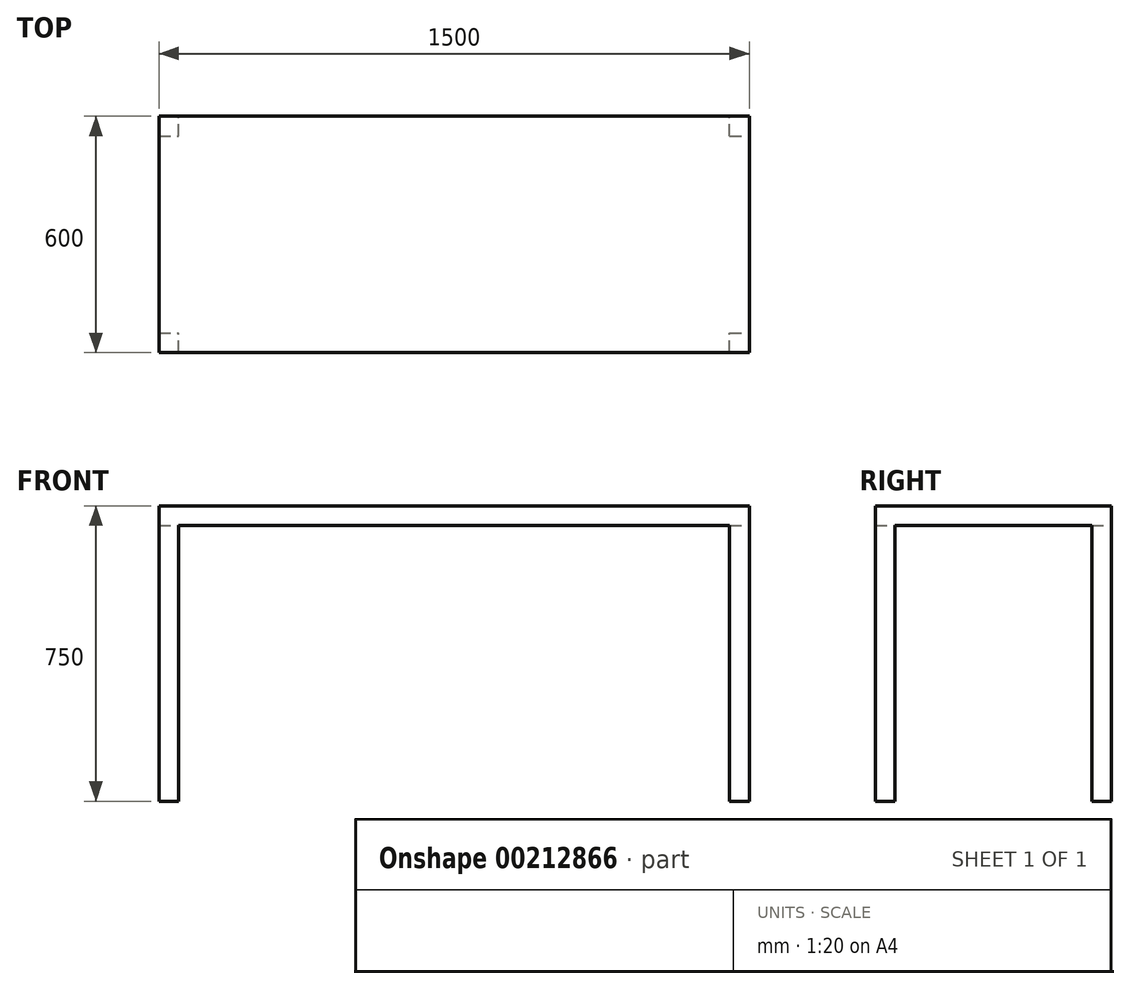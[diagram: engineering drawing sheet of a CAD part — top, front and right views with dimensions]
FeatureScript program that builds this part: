
annotation { "Feature Type Name" : "Feature", "Feature Type Description" : "" }
export const myFeature = defineFeature(function(context is Context, id is Id, definition is map)
    precondition{}
    {
        {
            var Q0;
            Q0=qCreatedBy(makeId("Top.planeOp"),FACE);
            var sketch = newSketch(context, id + "F0", { "sketchPlane" : qUnion([Q0])});
            skLineSegment(sketch, "E0.bottom", {"start": v(0, 600) * mm, "end": v(1500, 600) * mm});
            skLineSegment(sketch, "E0.top", {"start": v(0, 0) * mm, "end": v(1500, 0) * mm});
            skLineSegment(sketch, "E0.left", {"start": v(0, 600) * mm, "end": v(0, 0) * mm});
            skLineSegment(sketch, "E0.right", {"start": v(1500, 600) * mm, "end": v(1500, 0) * mm});
            skSolve(sketch);
        }
        {
            var Q0;
            Q0 = qSketchRegion(id + "F0", true);
            extrude(context, id + "F1", {"entities" : qUnion([Q0]), "depth" : 50 * mm});
        }
        {
            var Q0;
            Q0=makeQuery(id+"F1.opExtrude","CAP_FACE",FACE,{"disambiguationData":[OSD([sQuery(id+"F0.wireOp",EDGE,"E0.bottom"),sQuery(id+"F0.wireOp",EDGE,"E0.top"),sQuery(id+"F0.wireOp",EDGE,"E0.left"),sQuery(id+"F0.wireOp",EDGE,"E0.right")])],"isStart":true});
            var sketch = newSketch(context, id + "F2", { "sketchPlane" : qUnion([Q0])});
            skLineSegment(sketch, "E1.bottom", {"start": v(0, 0) * mm, "end": v(50, 0) * mm});
            skLineSegment(sketch, "E1.top", {"start": v(0, -50) * mm, "end": v(50, -50) * mm});
            skLineSegment(sketch, "E1.left", {"start": v(0, 0) * mm, "end": v(0, -50) * mm});
            skLineSegment(sketch, "E1.right", {"start": v(50, 0) * mm, "end": v(50, -50) * mm});
            skLineSegment(sketch, "E2.0.1.0", {"start": v(50, -550) * mm, "end": v(50, -600) * mm});
            skLineSegment(sketch, "E2.0.1.1", {"start": v(0, -550) * mm, "end": v(50, -550) * mm});
            skLineSegment(sketch, "E2.0.1.2", {"start": v(0, -550) * mm, "end": v(0, -600) * mm});
            skLineSegment(sketch, "E2.0.1.3", {"start": v(0, -600) * mm, "end": v(50, -600) * mm});
            skLineSegment(sketch, "E2.1.0.0", {"start": v(1500, 0) * mm, "end": v(1500, -50) * mm});
            skLineSegment(sketch, "E2.1.0.1", {"start": v(1450, 0) * mm, "end": v(1500, 0) * mm});
            skLineSegment(sketch, "E2.1.0.2", {"start": v(1450, 0) * mm, "end": v(1450, -50) * mm});
            skLineSegment(sketch, "E2.1.0.3", {"start": v(1450, -50) * mm, "end": v(1500, -50) * mm});
            skLineSegment(sketch, "E2.1.1.0", {"start": v(1500, -550) * mm, "end": v(1500, -600) * mm});
            skLineSegment(sketch, "E2.1.1.1", {"start": v(1450, -550) * mm, "end": v(1500, -550) * mm});
            skLineSegment(sketch, "E2.1.1.2", {"start": v(1450, -550) * mm, "end": v(1450, -600) * mm});
            skLineSegment(sketch, "E2.1.1.3", {"start": v(1450, -600) * mm, "end": v(1500, -600) * mm});
            skLineSegment(sketch, "E2.direction1", {"start": v(50, -50) * mm, "end": v(1500, -50) * mm, "construction": true});
            skLineSegment(sketch, "E2.direction2", {"start": v(50, -50) * mm, "end": v(50, -600) * mm, "construction": true});
            skSolve(sketch);
        }
        {
            var Q0;
            Q0=makeQuery(id+"F2.imprint","IMPRINT",FACE,{"disambiguationData":[TD([[makeQuery(id+"F2.imprint","IMPRINT",EDGE,{"derivedFrom":sQuery(id+"F2.wireOp",EDGE,"E1.bottom")}),-1.0]])]});
            var Q1;
            Q1=makeQuery(id+"F2.imprint","IMPRINT",FACE,{"disambiguationData":[TD([[makeQuery(id+"F2.imprint","IMPRINT",EDGE,{"derivedFrom":sQuery(id+"F2.wireOp",EDGE,"E2.0.1.0")}),-1.0]])]});
            var Q2;
            Q2=makeQuery(id+"F2.imprint","IMPRINT",FACE,{"disambiguationData":[TD([[makeQuery(id+"F2.imprint","IMPRINT",EDGE,{"derivedFrom":sQuery(id+"F2.wireOp",EDGE,"E2.1.1.0")}),1.0]])]});
            var Q3;
            Q3=makeQuery(id+"F2.imprint","IMPRINT",FACE,{"disambiguationData":[TD([[makeQuery(id+"F2.imprint","IMPRINT",EDGE,{"derivedFrom":sQuery(id+"F2.wireOp",EDGE,"E2.1.0.0")}),1.0]])]});
            extrude(context, id + "F3", {"entities" : qUnion([Q0, Q1, Q2, Q3]), "operationType" : NewBodyOperationType.ADD, "depth" : 700 * mm});
        }
    });
